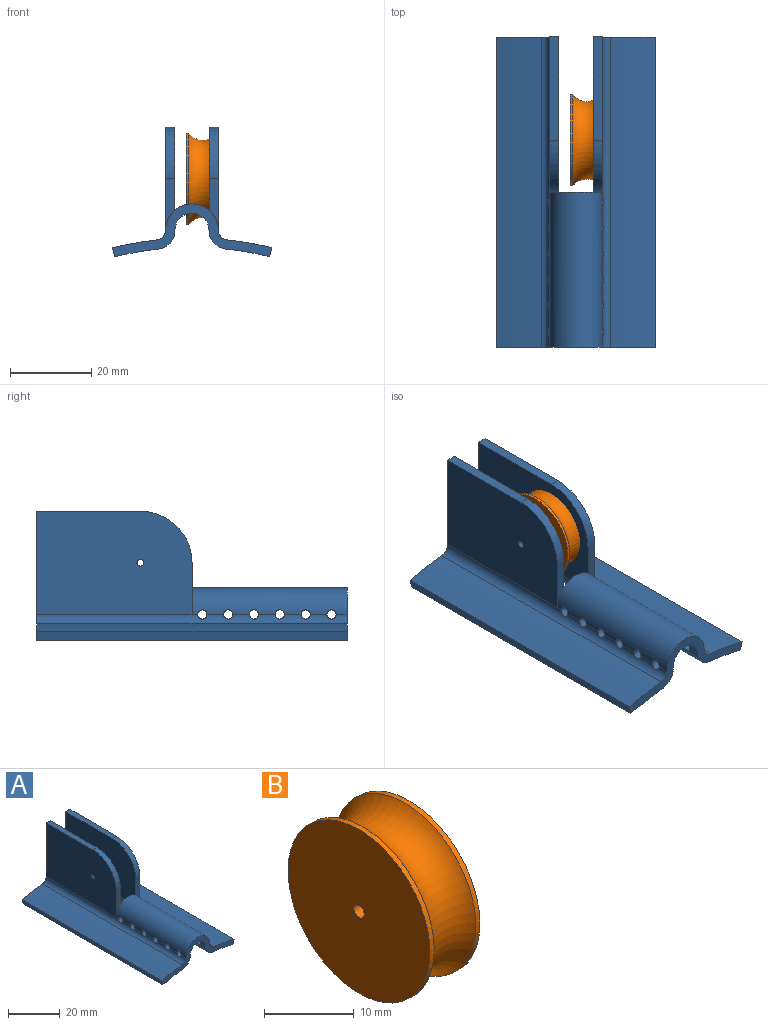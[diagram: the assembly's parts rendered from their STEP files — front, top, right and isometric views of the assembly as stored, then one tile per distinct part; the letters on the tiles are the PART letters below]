
ASSEMBLY  parts=2 mates=1
PART A: 56 faces, bbox 39.2x76.2x31.9 mm
  f0: plane 8.39x6.48mm, normal (0,1,0), area 22.6mm2, adj f1,f2,f44,f49
  f1: cylinder r=4.19mm len=38.1mm, axis (0,-1,0), area 478.4mm2, adj f0,f6,f7,f8,f9,f10,f11,f12
  f2: cylinder r=6.48mm len=38.1mm, axis (0,-1,0), area 754.9mm2, adj f0,f19,f20,f29,f30,f31,f32,f33
  f3: plane 31.84x15.41mm, normal (0,1,0), area 94.9mm2, adj f18,f19,f24,f25,f26,f27,f43,f44
  f4: plane 31.85x15.44mm, normal (0,1,0), area 95mm2, adj f5,f20,f21,f22,f23,f28,f49,f50
  f5: cylinder r=4.57mm len=76.2mm, axis (0,-1,0), area 498.7mm2, adj f4,f6,f7,f8,f9,f10,f11,f22
  f6: plane 2.67x0.08mm, normal (1,0,0), area 0.2mm2, adj f1,f5,f29,f35
  f7: plane 4.07x0.08mm, normal (1,0,0), area 0.3mm2, adj f1,f5,f34,f35
  f8: plane 4.07x0.08mm, normal (1,0,0), area 0.3mm2, adj f1,f5,f33,f34
  f9: plane 4.07x0.08mm, normal (1,0,0), area 0.3mm2, adj f1,f5,f32,f33
  f10: plane 4.07x0.08mm, normal (1,0,0), area 0.3mm2, adj f1,f5,f31,f32
  f11: plane 4.07x0.08mm, normal (1,0,0), area 0.3mm2, adj f1,f5,f30,f31
  f12: plane 2.67x0.08mm, normal (-1,0,0), area 0.2mm2, adj f1,f18,f29,f41
  f13: plane 4.07x0.08mm, normal (-1,0,0), area 0.3mm2, adj f1,f18,f40,f41
  f14: plane 4.07x0.08mm, normal (-1,0,0), area 0.3mm2, adj f1,f18,f39,f40
  f15: plane 4.07x0.08mm, normal (-1,0,0), area 0.3mm2, adj f1,f18,f38,f39
  f16: plane 4.07x0.08mm, normal (-1,0,0), area 0.3mm2, adj f1,f18,f37,f38
  f17: plane 4.07x0.08mm, normal (-1,0,0), area 0.3mm2, adj f1,f18,f36,f37
  f18: cylinder r=4.57mm len=76.2mm, axis (0,-1,0), area 498.7mm2, adj f3,f12,f13,f14,f15,f16,f17,f24
  f19: cylinder r=2.29mm len=76.2mm, axis (0,-1,0), area 243.6mm2, adj f2,f3,f27,f29,f36,f37,f38,f39
  f20: cylinder r=2.29mm len=76.2mm, axis (0,-1,0), area 244.2mm2, adj f2,f4,f28,f29,f30,f31,f32,f33
  f21: plane 76.2x2.22mm, normal (-0.97,0,-0.24), area 174.2mm2, adj f4,f22,f28,f29
  f22: cylinder r=79.38mm len=76.2mm, axis (0,-1,0), area 833.4mm2, adj f4,f5,f21,f29
  f23: plane 39.5x0.08mm, normal (1,0,0), area 0.8mm2, adj f1,f4,f5,f30,f48,f49
  f24: plane 39.5x0.08mm, normal (-1,0,0), area 0.3mm2, adj f1,f3,f18,f36,f44
  f25: cylinder r=79.38mm len=76.2mm, axis (0,-1,0), area 833.4mm2, adj f3,f18,f26,f29
  f26: plane 76.2x2.22mm, normal (0.97,0,-0.24), area 174.2mm2, adj f3,f25,f27,f29
  f27: cylinder r=81.66mm len=76.2mm, axis (0,-1,0), area 857.4mm2, adj f3,f19,f26,f29
  f28: cylinder r=81.66mm len=76.2mm, axis (0,-1,0), area 857.4mm2, adj f4,f20,f21,f29
  f29: plane 39.2x12.99mm, normal (0,-1,0), area 112.4mm2, adj f1,f2,f5,f6,f12,f18,f19,f20
  f30: cylinder r=1.14mm len=2.72mm, axis (-1,0,0), area 16.8mm2, adj f1,f2,f5,f11,f20,f23
  f31: cylinder r=1.14mm len=2.72mm, axis (-1,0,0), area 16.8mm2, adj f1,f2,f5,f10,f11,f20
  f32: cylinder r=1.14mm len=2.72mm, axis (-1,0,0), area 16.8mm2, adj f1,f2,f5,f9,f10,f20
  f33: cylinder r=1.14mm len=2.72mm, axis (-1,0,0), area 16.8mm2, adj f1,f2,f5,f8,f9,f20
  f34: cylinder r=1.14mm len=2.72mm, axis (-1,0,0), area 16.8mm2, adj f1,f2,f5,f7,f8,f20
  f35: cylinder r=1.14mm len=2.72mm, axis (-1,0,0), area 16.8mm2, adj f1,f2,f5,f6,f7,f20
  f36: cylinder r=1.14mm len=2.72mm, axis (-1,0,0), area 16.8mm2, adj f1,f2,f17,f18,f19,f24
  f37: cylinder r=1.14mm len=2.72mm, axis (-1,0,0), area 16.8mm2, adj f1,f2,f16,f17,f18,f19
  f38: cylinder r=1.14mm len=2.72mm, axis (-1,0,0), area 16.8mm2, adj f1,f2,f15,f16,f18,f19
  f39: cylinder r=1.14mm len=2.72mm, axis (-1,0,0), area 16.8mm2, adj f1,f2,f14,f15,f18,f19
  f40: cylinder r=1.14mm len=2.72mm, axis (-1,0,0), area 16.8mm2, adj f1,f2,f13,f14,f18,f19
  f41: cylinder r=1.14mm len=2.72mm, axis (-1,0,0), area 16.8mm2, adj f1,f2,f12,f13,f18,f19
  f42: plane 0.11x0mm, normal (0,1,0), area 0mm2, adj f2,f43
  f43: plane 38.1x25.4mm, normal (1,0,0), area 931mm2, adj f3,f19,f42,f45,f46,f53,f55
  f44: plane 38.1x25.4mm, normal (-1,0,0), area 931mm2, adj f0,f3,f24,f45,f46,f53,f55
  f45: plane 12.58x2.3mm, normal (0,-1,0), area 21mm2, adj f2,f43,f44,f53
  f46: plane 25.4x2.29mm, normal (0,0,1), area 58.1mm2, adj f3,f43,f44,f53
  f47: plane 12.57x2.3mm, normal (0,-1,0), area 21mm2, adj f2,f49,f50,f52
  f48: plane 0.06x0mm, normal (0,-1,0), area 0mm2, adj f23,f49
  f49: plane 38.1x25.4mm, normal (1,0,0), area 931mm2, adj f0,f1,f4,f23,f47,f48,f51,f52
  f50: plane 38.1x25.4mm, normal (-1,0,0), area 931mm2, adj f2,f4,f20,f47,f51,f52,f54
  f51: plane 25.4x2.29mm, normal (0,0,1), area 58.1mm2, adj f4,f49,f50,f52
  f52: cylinder r=12.7mm len=12.7mm, axis (-1,0,0), area 45.6mm2, adj f47,f49,f50,f51
  f53: cylinder r=12.7mm len=12.7mm, axis (-1,0,0), area 45.6mm2, adj f43,f44,f45,f46
  f54: cylinder r=0.83mm len=2.29mm, axis (1,0,0), area 11.9mm2, adj f49,f50
  f55: cylinder r=0.83mm len=2.29mm, axis (1,0,0), area 11.9mm2, adj f43,f44
PART B: 6 faces, bbox 8.1x29.4x29.4 mm
  f0: cylinder r=11.19mm len=22.39mm, axis (1,0,0), area 46mm2, adj f1,f4
  f1: torus R=13.59mm, axis (1,0,0), area 484.9mm2, adj f0,f2
  f2: cylinder r=11.19mm len=22.39mm, axis (1,0,0), area 46mm2, adj f1,f3
  f3: plane 22.39x22.39mm, normal (-1,0,0), area 391.5mm2, adj f2,f5
  f4: plane 22.39x22.39mm, normal (1,0,0), area 391.5mm2, adj f0,f5
  f5: cylinder r=0.83mm len=7.87mm, axis (-1,0,0), area 40.8mm2, adj f3,f4
PLACE A rot(axis=(0,-1,0),0.1deg) t=(-14.16,-19.72,10.26)mm
PLACE B t=(-11.63,31.08,29.41)mm
MATE cylindrical A.f52 <-> B.f5  axis (1,0,0) through (-7.69,31.08,29.41)mm
